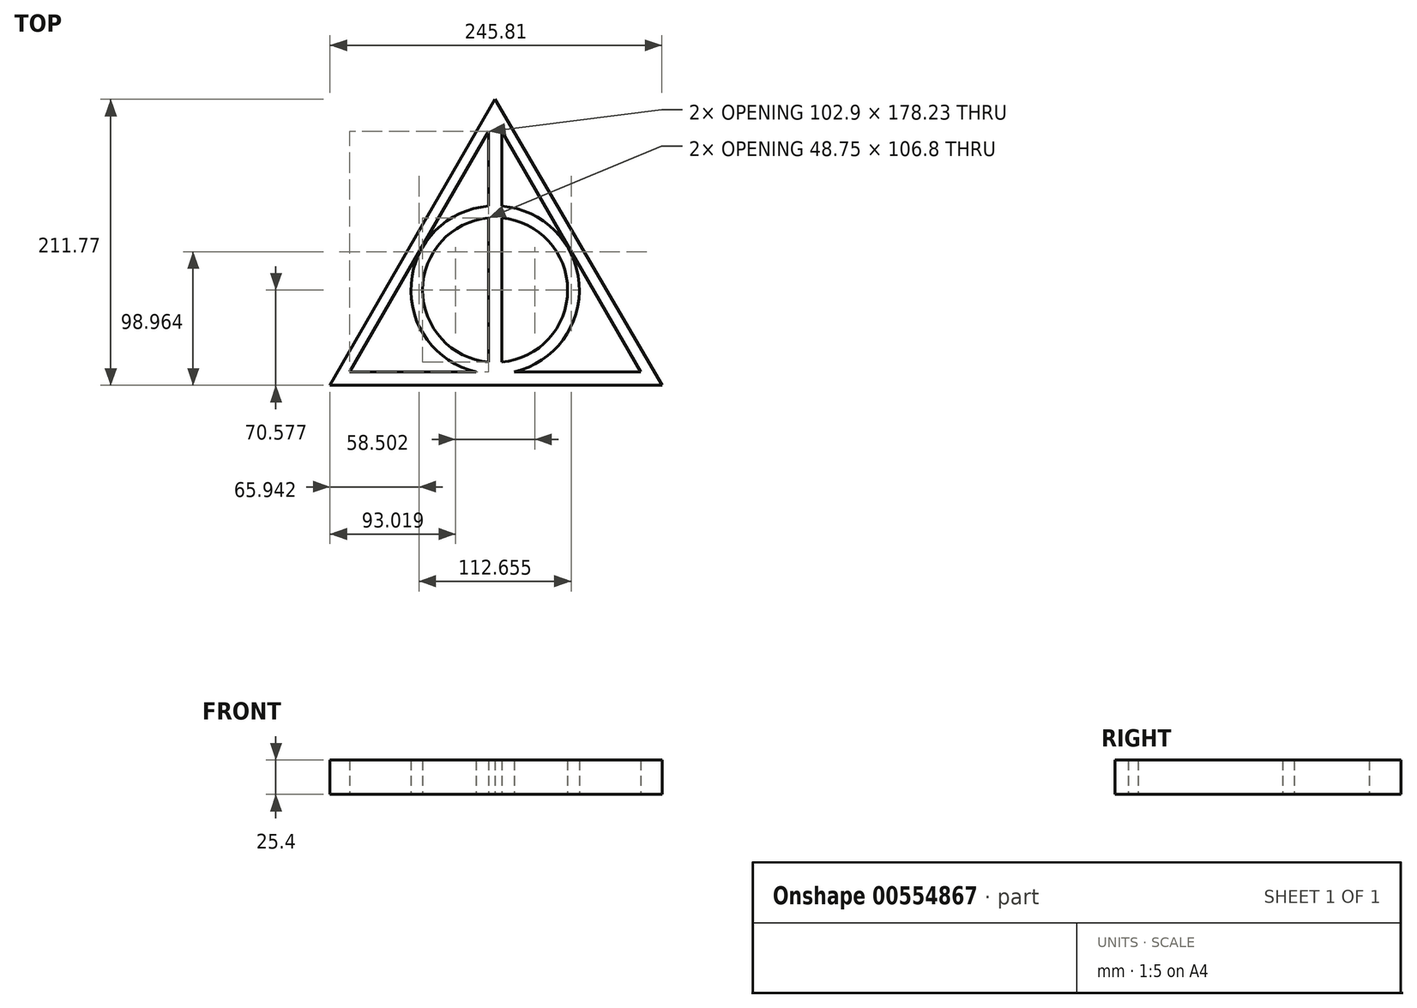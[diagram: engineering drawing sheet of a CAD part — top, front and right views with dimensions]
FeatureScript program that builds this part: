
annotation { "Feature Type Name" : "Feature", "Feature Type Description" : "" }
export const myFeature = defineFeature(function(context is Context, id is Id, definition is map)
    precondition{}
    {
        {
            var Q0;
            Q0=qCreatedBy(makeId("Top.planeOp"),FACE);
            var sketch = newSketch(context, id + "F0", { "sketchPlane" : qUnion([Q0])});
            skLineSegment(sketch, "E0", {"start": v(0, 186.68) * mm, "end": v(-107.78, 0) * mm});
            skLineSegment(sketch, "E1", {"start": v(-107.78, 0) * mm, "end": v(107.78, 0) * mm});
            skLineSegment(sketch, "E2", {"start": v(107.78, 0) * mm, "end": v(0, 186.68) * mm});
            skLineSegment(sketch, "E3", {"start": v(0, 201.92) * mm, "end": v(-122.27, -9.85) * mm});
            skLineSegment(sketch, "E4", {"start": v(-122.27, -9.85) * mm, "end": v(123.54, -9.85) * mm});
            skLineSegment(sketch, "E5", {"start": v(123.54, -9.85) * mm, "end": v(0, 201.92) * mm});
            skCircle(sketch, "E6", {"center": v(0, 60.73) * mm, "radius": 62.35 * mm});
            skCircle(sketch, "E7", {"center": v(0, 60.73) * mm, "radius": 53.62 * mm});
            skLineSegment(sketch, "E8", {"start": v(-4.88, 178.23) * mm, "end": v(-4.88, 0) * mm});
            skLineSegment(sketch, "E9", {"start": v(4.88, 178.23) * mm, "end": v(4.88, -1.43) * mm});
            skSolve(sketch);
        }
        {
            var Q0;
            {var subQ1=sQuery(id+"F0.wireOp",EDGE,"E0");var subQ7=sQuery(id+"F0.wireOp",EDGE,"E2");var subQ8=makeQuery(id+"F0.imprint","INTERSECT",VERTEX,{"derivedFrom":[subQ1,subQ7]});Q0=makeQuery(id+"F0.imprint","IMPRINT",FACE,{"disambiguationData":[TD([[makeQuery(id+"F0.imprint","IMPRINT",EDGE,{"disambiguationData":[TD([[subQ8,-1.0]])],"derivedFrom":subQ1}),1.0]])]});}
            var Q1;
            {var subQ0=sQuery(id+"F0.wireOp",EDGE,"E8");var subQ6=sQuery(id+"F0.wireOp",EDGE,"E1");var subQ8=makeQuery(id+"F0.imprint","INTERSECT",VERTEX,{"derivedFrom":[subQ6,subQ0]});Q1=makeQuery(id+"F0.imprint","IMPRINT",FACE,{"disambiguationData":[TD([[makeQuery(id+"F0.imprint","IMPRINT",EDGE,{"disambiguationData":[TD([[subQ8,1.0]])],"derivedFrom":subQ6}),1.0]])]});}
            var Q2;
            {var subQ0=sQuery(id+"F0.wireOp",EDGE,"E8");var subQ1=sQuery(id+"F0.wireOp",EDGE,"E7");var subQ2=makeQuery(id+"F0.imprint","INTERSECT",VERTEX,{"disambiguationData":[OD(0.0)],"derivedFrom":[subQ1,subQ0]});Q2=makeQuery(id+"F0.imprint","IMPRINT",FACE,{"disambiguationData":[TD([[makeQuery(id+"F0.imprint","IMPRINT",EDGE,{"disambiguationData":[TD([[subQ2,1.0]])],"derivedFrom":subQ1}),1.0]])]});}
            var Q3;
            {var subQ0=sQuery(id+"F0.wireOp",EDGE,"E8");var subQ1=sQuery(id+"F0.wireOp",EDGE,"E6");var subQ2=makeQuery(id+"F0.imprint","INTERSECT",VERTEX,{"derivedFrom":[subQ1,subQ0]});Q3=makeQuery(id+"F0.imprint","IMPRINT",FACE,{"disambiguationData":[TD([[makeQuery(id+"F0.imprint","IMPRINT",EDGE,{"disambiguationData":[TD([[subQ2,1.0]])],"derivedFrom":subQ1}),1.0]])]});}
            var Q4;
            {var subQ0=sQuery(id+"F0.wireOp",EDGE,"E9");var subQ5=sQuery(id+"F0.wireOp",EDGE,"E1");var subQ7=makeQuery(id+"F0.imprint","INTERSECT",VERTEX,{"derivedFrom":[subQ5,subQ0]});Q4=makeQuery(id+"F0.imprint","IMPRINT",FACE,{"disambiguationData":[TD([[makeQuery(id+"F0.imprint","IMPRINT",EDGE,{"disambiguationData":[TD([[subQ7,-1.0]])],"derivedFrom":subQ5}),1.0]])]});}
            var Q5;
            {var subQ0=sQuery(id+"F0.wireOp",EDGE,"E8");var subQ1=sQuery(id+"F0.wireOp",EDGE,"E1");var subQ2=makeQuery(id+"F0.imprint","INTERSECT",VERTEX,{"derivedFrom":[subQ1,subQ0]});Q5=makeQuery(id+"F0.imprint","IMPRINT",FACE,{"disambiguationData":[TD([[makeQuery(id+"F0.imprint","IMPRINT",EDGE,{"disambiguationData":[TD([[subQ2,-1.0]])],"derivedFrom":subQ1}),1.0]])]});}
            var Q6;
            {var subQ0=sQuery(id+"F0.wireOp",EDGE,"E1");var subQ1=makeQuery(id+"F0.imprint","INTERSECT",VERTEX,{"derivedFrom":[subQ0,sQuery(id+"F0.wireOp",EDGE,"E8")]});Q6=makeQuery(id+"F0.imprint","IMPRINT",FACE,{"disambiguationData":[TD([[makeQuery(id+"F0.imprint","IMPRINT",EDGE,{"disambiguationData":[TD([[subQ1,1.0]])],"derivedFrom":subQ0}),-1.0]])]});}
            var Q7;
            Q7=makeQuery(id+"F0.imprint","IMPRINT",FACE,{"disambiguationData":[TD([[makeQuery(id+"F0.imprint","IMPRINT",EDGE,{"derivedFrom":sQuery(id+"F0.wireOp",EDGE,"E3")}),1.0]])]});
            var Q8;
            {var subQ0=sQuery(id+"F0.wireOp",EDGE,"E9");var subQ1=sQuery(id+"F0.wireOp",EDGE,"E1");var subQ2=makeQuery(id+"F0.imprint","INTERSECT",VERTEX,{"derivedFrom":[subQ1,subQ0]});Q8=makeQuery(id+"F0.imprint","IMPRINT",FACE,{"disambiguationData":[TD([[makeQuery(id+"F0.imprint","IMPRINT",EDGE,{"disambiguationData":[TD([[subQ2,-1.0]])],"derivedFrom":subQ1}),-1.0]])]});}
            extrude(context, id + "F1", {"entities" : qUnion([Q0, Q1, Q2, Q3, Q4, Q5, Q6, Q7, Q8]), "depth" : 25.4 * mm, "offsetDistance" : 25.4 * mm});
        }
    });
